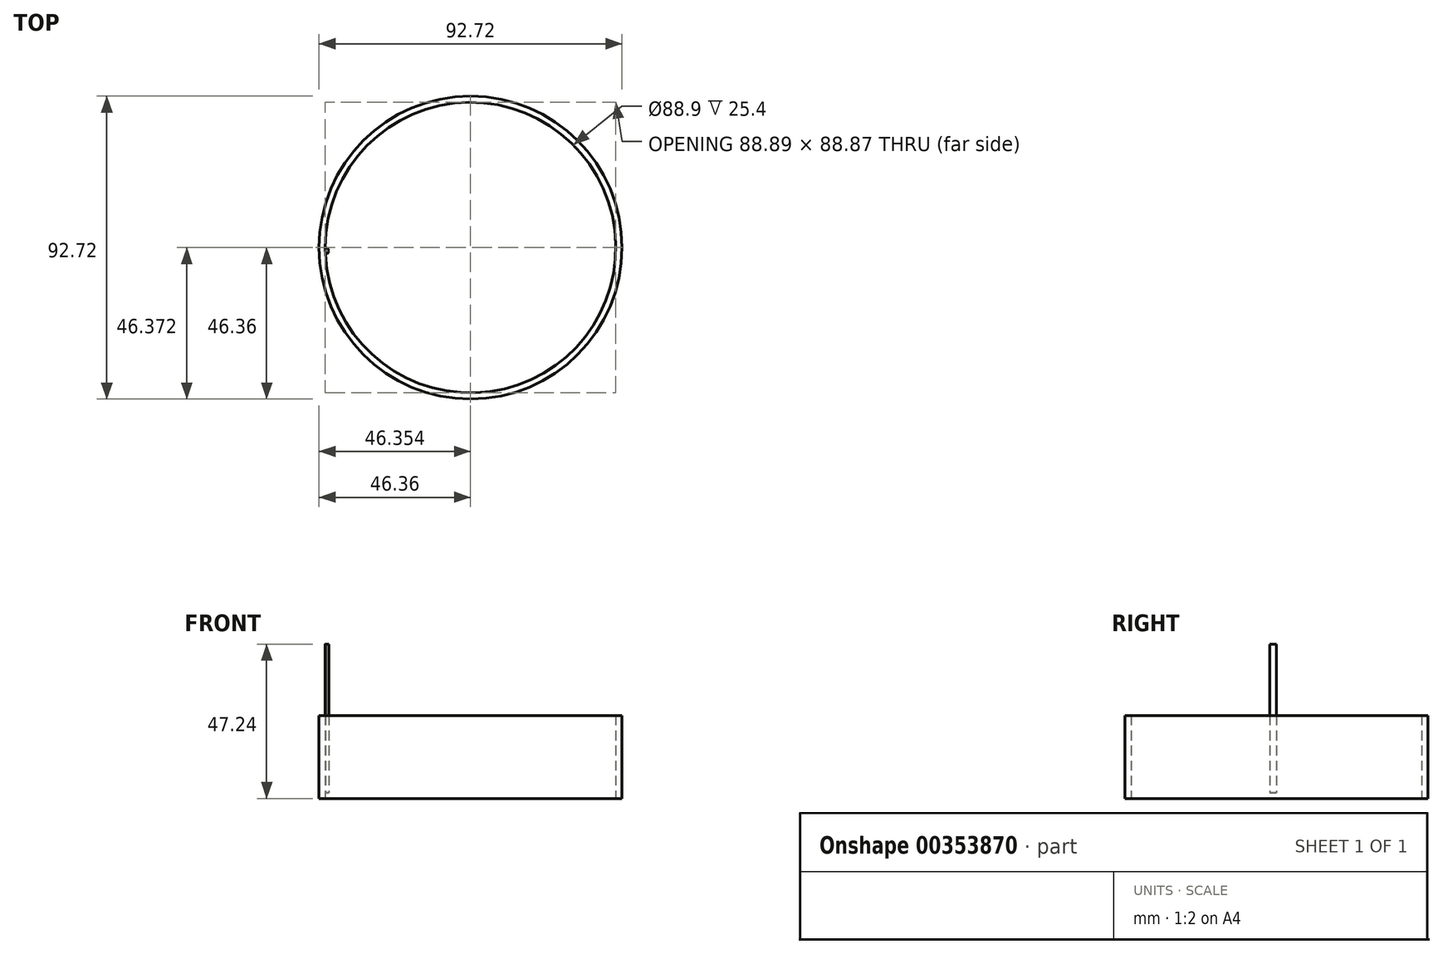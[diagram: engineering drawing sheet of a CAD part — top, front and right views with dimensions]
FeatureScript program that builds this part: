
annotation { "Feature Type Name" : "Feature", "Feature Type Description" : "" }
export const myFeature = defineFeature(function(context is Context, id is Id, definition is map)
    precondition{}
    {
        {
            var Q0;
            Q0=qCreatedBy(makeId("Top.planeOp"),FACE);
            var sketch = newSketch(context, id + "F0", { "sketchPlane" : qUnion([Q0])});
            skCircle(sketch, "E0", {"center": v(0, 0) * mm, "radius": 44.45 * mm});
            skCircle(sketch, "E1", {"center": v(0, 0) * mm, "radius": 46.35 * mm});
            skCircle(sketch, "E2", {"center": v(0, 0) * mm, "radius": 2.86 * mm});
            skArc(sketch, "E3", {"start": v(-44.4, -2.03) * mm, "mid": v(-43.41, -1) * mm, "end": v(-44.45, 0) * mm});
            skSolve(sketch);
        }
        {
            var Q0;
            Q0=makeQuery(id+"F0.imprint","IMPRINT",FACE,{"disambiguationData":[TD([[makeQuery(id+"F0.imprint","IMPRINT",EDGE,{"derivedFrom":sQuery(id+"F0.wireOp",EDGE,"E0")}),-1.0]])]});
            extrude(context, id + "F1", {"entities" : qUnion([Q0]), "depth" : 25.4 * mm});
        }
        {
            var Q0;
            Q0=makeQuery(id+"F0.imprint","IMPRINT",FACE,{"disambiguationData":[TD([[makeQuery(id+"F0.imprint","IMPRINT",EDGE,{"derivedFrom":sQuery(id+"F0.wireOp",EDGE,"E0")}),1.0]])]});
            extrude(context, id + "F2", {"entities" : qUnion([Q0]), "operationType" : NewBodyOperationType.ADD, "depth" : 23.62 * mm, "hasSecondDirection" : true, "secondDirectionOppositeDirection" : false, "secondDirectionDepth" : 1.78 * mm});
        }
        {
            var Q0;
            Q0=makeQuery(id+"F2.opExtrude","CAP_FACE",FACE,{"disambiguationData":[OSD([sQuery(id+"F0.wireOp",EDGE,"E0"),sQuery(id+"F0.wireOp",EDGE,"E3")])],"isStart":false});
            extrude(context, id + "F3", {"entities" : qUnion([Q0]), "operationType" : NewBodyOperationType.ADD, "depth" : 23.62 * mm, "hasSecondDirection" : true, "secondDirectionOppositeDirection" : true, "secondDirectionDepth" : 1.78 * mm});
        }
    });
